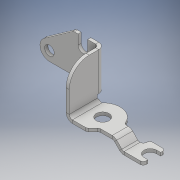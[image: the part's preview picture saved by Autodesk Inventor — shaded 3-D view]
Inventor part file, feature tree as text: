
AUTODESK INVENTOR PART (.ipt)
format: ipt  version: 2018 (Build 220112000, 112)  size: 320,000 bytes
history: native  units: mm
features: sheet_metal_op x10, other x5, sketch x4, plane x2, chamfer x2
ambient origin geometry x8: Origin, YZ Plane, XZ Plane, XY Plane, X Axis, Y Axis, Z Axis, Center Point
bodies: Solid1 (feature_tree)
feature tree (23):
  sheet_metal_op  "Face1"
  plane  "Work Plane1"
  sheet_metal_op  "Face3"
  sheet_metal_op  "Bend4"
  sheet_metal_op  "Flange2"
  plane  "Work Plane2"
  sheet_metal_op  "Face4"
  sheet_metal_op  "Bend8"
  chamfer  "Corner Round1"
  chamfer  "Corner Round2"
  sketch  "Sketch1"  dims[d0=18.0mm]
  other  "Plate1"
  sketch  "Sketch4"  dims[d1=24.0mm]
  other  "Plate3"
  sheet_metal_op  "Bend3"
  sketch  "Sketch6"  dims[d2=8.0mm]
  other  "Plate5"
  sheet_metal_op  "Bend6"
  sheet_metal_op  "Corner2"
  sketch  "Sketch7"  dims[d3=45.0deg d4=20.0mm d5=90.0deg d6=22.0mm d7=16.0mm d8=16.0mm d9=22.0mm d10=4.0mm d30=6.0mm d31=60.0mm d32=8.0mm d33=180.0deg d34=5.0mm d35=5.0mm d36=20.0mm d37=14.0mm d38=14.0mm d39=4.0mm d40=4.0mm d41=2.0mm d42=8.0mm d43=4.0mm d44=4.0mm d45=2.0mm d46=8.0mm d47=4.0mm d48=4.0mm d59=4.0mm d60=2.0mm d61=8.0mm d62=4.0mm d63=60.0mm d64=90.0deg d65=4.0mm d66=16.0mm d67=4.0mm d68=4.0mm d69=4.0mm d71=6.0mm d72=180.0deg d73=24.0mm d74=12.0mm d75=0.0mm d76=6.0mm d80=12.0mm d81=12.0mm d82=4.0mm d83=4.0mm d84=2.0mm d85=8.0mm d86=4.0mm d88=48.0mm d89=66.0mm d90=4.0mm d91=2.0mm d92=8.0mm d93=4.0mm d94=4.0mm d95=25.0mm d96=4.0mm]
  other  "Plate6"
  sheet_metal_op  "Bend7"
  other  "Definition1"
